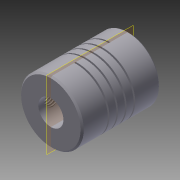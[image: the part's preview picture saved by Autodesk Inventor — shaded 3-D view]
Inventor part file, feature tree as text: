
AUTODESK INVENTOR PART (.ipt)
format: ipt  version: 2015 (Build 190159000, 159)  size: 226,304 bytes
history: native  units: mm
features: hole x2, revolve x1, other x1, chamfer x1, projected_geometry x1
ambient origin geometry x8: Origin, YZ Plane, XZ Plane, XY Plane, X Axis, Y Axis, Z Axis, Center Point
bodies: Solid1 (feature_tree)
feature tree (6):
  revolve  "Revolución1"  [1 undecoded]
  other  "Espira1"
  hole  "Agujero1"  [1 undecoded]
  chamfer  "Chaflán1"  Distance=8.0mm
  hole  "Agujero2"  [1 undecoded]
  projected_geometry  "Contorno proyectado1"
note: 3 required parameter values undecoded (feature->parameter linkage not recoverable at this tier; creation-order binding heuristic only, values carry confidence <= 0.55)